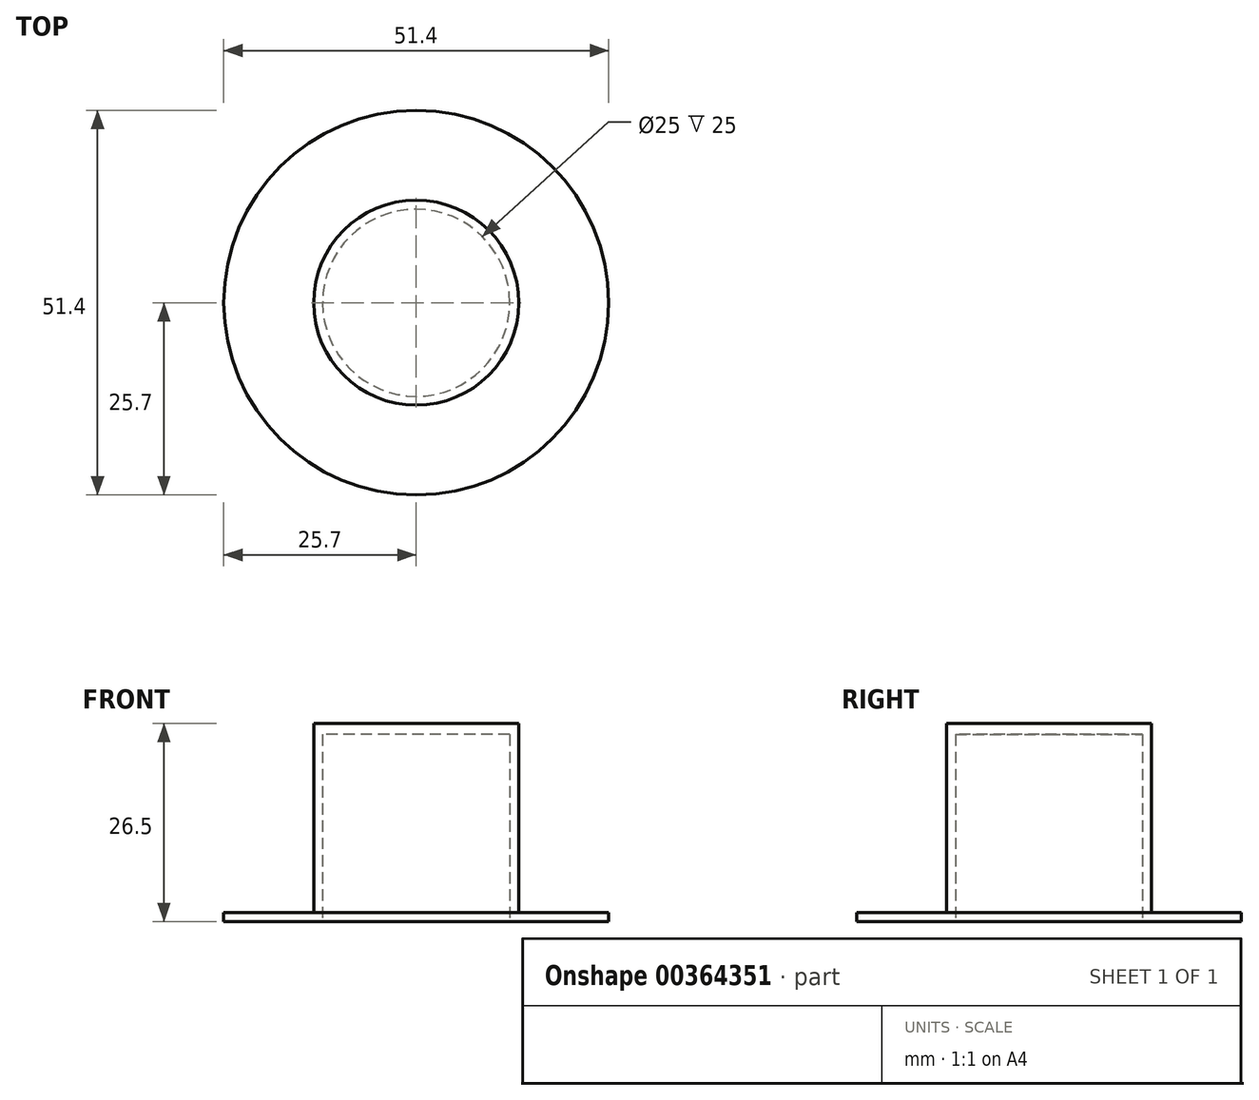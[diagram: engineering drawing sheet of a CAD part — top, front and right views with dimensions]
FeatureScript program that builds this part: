
annotation { "Feature Type Name" : "Feature", "Feature Type Description" : "" }
export const myFeature = defineFeature(function(context is Context, id is Id, definition is map)
    precondition{}
    {
        {
            var Q0;
            Q0=qCreatedBy(makeId("Top.planeOp"),FACE);
            var sketch = newSketch(context, id + "F0", { "sketchPlane" : qUnion([Q0])});
            skCircle(sketch, "E0", {"center": v(0, 0) * mm, "radius": 12.5 * mm});
            skCircle(sketch, "E1", {"center": v(0, 0) * mm, "radius": 13.7 * mm});
            skSolve(sketch);
        }
        {
            var Q0;
            Q0 = qSketchRegion(id + "F0", true);
            extrude(context, id + "F1", {"entities" : qUnion([Q0]), "depth" : 25 * mm});
        }
        {
            var Q0;
            Q0=makeQuery(id+"F1.opExtrude","CAP_FACE",FACE,{"disambiguationData":[OSD([sQuery(id+"F0.wireOp",EDGE,"E0"),sQuery(id+"F0.wireOp",EDGE,"E1")])],"isStart":false});
            var sketch = newSketch(context, id + "F2", { "sketchPlane" : qUnion([Q0])});
            skCircle(sketch, "E2.0", {"center": v(0, 0) * mm, "radius": 13.7 * mm});
            skSolve(sketch);
        }
        {
            var Q0;
            Q0 = qSketchRegion(id + "F2", true);
            extrude(context, id + "F3", {"entities" : qUnion([Q0]), "operationType" : NewBodyOperationType.ADD, "depth" : 1.5 * mm});
        }
        {
            var Q0;
            Q0=makeQuery(id+"F1.opExtrude","CAP_FACE",FACE,{"disambiguationData":[OSD([sQuery(id+"F0.wireOp",EDGE,"E0"),sQuery(id+"F0.wireOp",EDGE,"E1")])],"isStart":true});
            var sketch = newSketch(context, id + "F4", { "sketchPlane" : qUnion([Q0])});
            skLineSegment(sketch, "E3.0", {"start": v(-12.5, 0) * mm, "end": v(12.5, 0) * mm});
            skCircle(sketch, "E4", {"center": v(0, 0) * mm, "radius": 25.7 * mm});
            skSolve(sketch);
        }
        {
            var Q0;
            Q0=makeQuery(id+"F4.imprint","IMPRINT",FACE,{"disambiguationData":[TD([[makeQuery(id+"F4.imprint","IMPRINT",EDGE,{"derivedFrom":sQuery(id+"F4.wireOp",EDGE,"E4")}),1.0]])]});
            var Q1;
            Q1=makeQuery(id+"F4.imprint","IMPRINT",FACE,{"disambiguationData":[TD([[makeQuery(id+"F4.imprint","IMPRINT",EDGE,{"derivedFrom":makeQuery(id+"F1.opExtrude","CAP_EDGE",EDGE,{"disambiguationData":[OSD([sQuery(id+"F0.wireOp",EDGE,"E1")])],"isStart":true})}),-1.0]])]});
            extrude(context, id + "F5", {"entities" : qUnion([Q0, Q1]), "operationType" : NewBodyOperationType.ADD, "oppositeDirection" : true, "depth" : 1.2 * mm});
        }
    });
